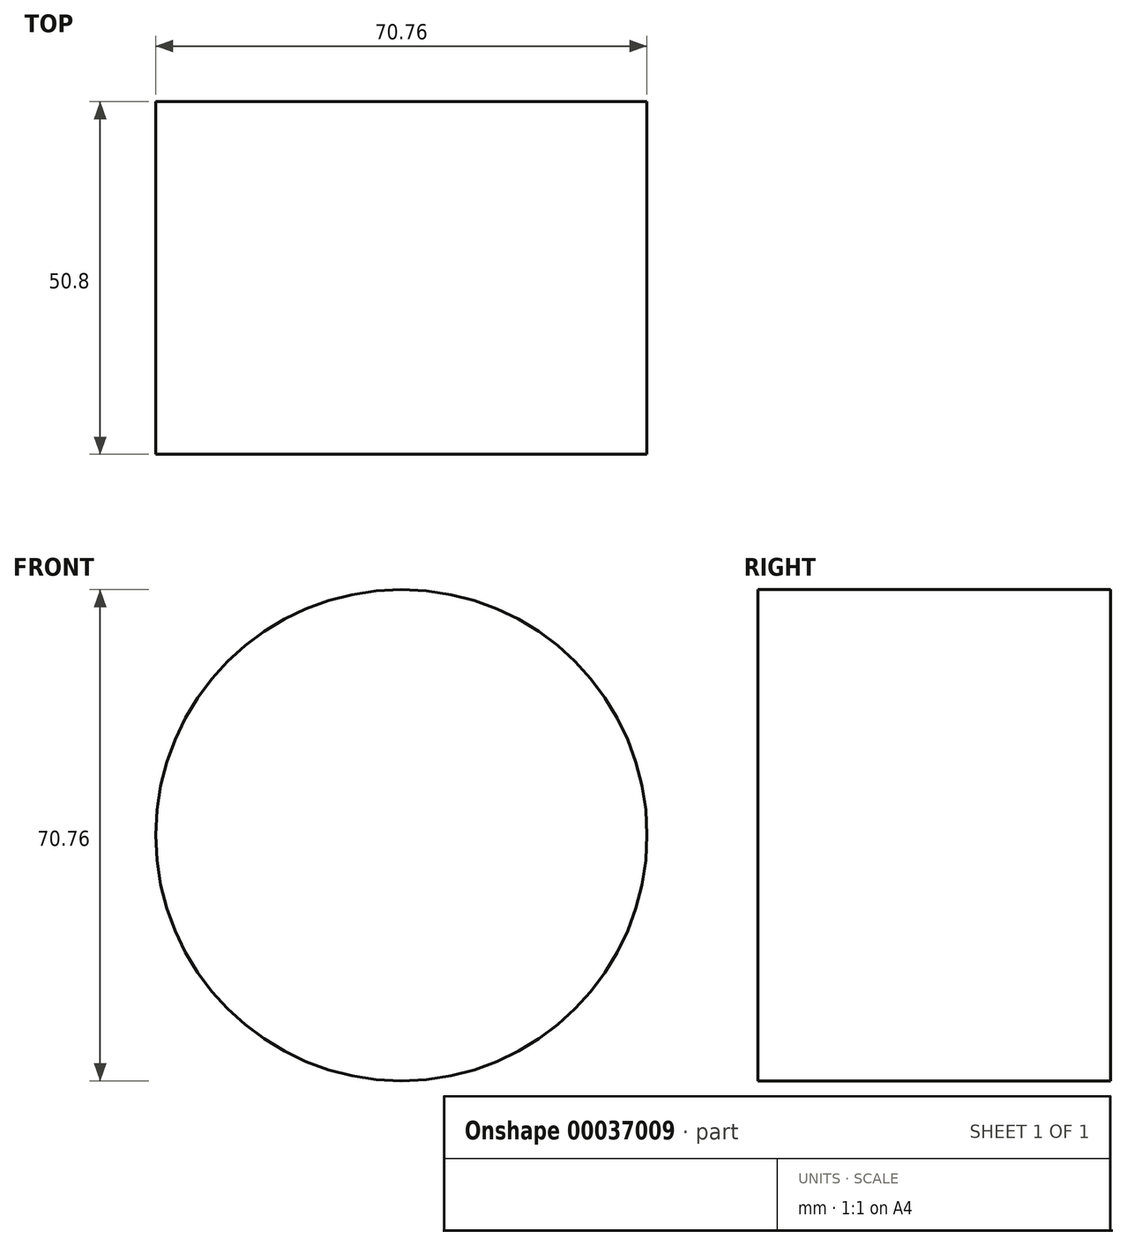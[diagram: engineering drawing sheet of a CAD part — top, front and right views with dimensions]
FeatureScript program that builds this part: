
annotation { "Feature Type Name" : "Feature", "Feature Type Description" : "" }
export const myFeature = defineFeature(function(context is Context, id is Id, definition is map)
    precondition{}
    {
        {
            var Q0;
            Q0=qCreatedBy(makeId("Front.planeOp"),FACE);
            var sketch = newSketch(context, id + "F0", { "sketchPlane" : qUnion([Q0])});
            skCircle(sketch, "E0", {"center": v(0, 0) * mm, "radius": 35.38 * mm});
            skCircle(sketch, "E1.cCircle", {"center": v(0, 0) * mm, "radius": 29.9 * mm, "construction": true});
            skLineSegment(sketch, "E1.0", {"start": v(17.26, -29.9) * mm, "end": v(-17.26, -29.9) * mm});
            skLineSegment(sketch, "E1.1", {"start": v(-17.26, -29.9) * mm, "end": v(-34.53, 0) * mm});
            skLineSegment(sketch, "E1.2", {"start": v(-34.53, 0) * mm, "end": v(-17.26, 29.9) * mm});
            skLineSegment(sketch, "E1.3", {"start": v(-17.26, 29.9) * mm, "end": v(17.26, 29.9) * mm});
            skLineSegment(sketch, "E1.4", {"start": v(17.26, 29.9) * mm, "end": v(34.53, 0) * mm});
            skLineSegment(sketch, "E1.5", {"start": v(34.53, 0) * mm, "end": v(17.26, -29.9) * mm});
            skPoint(sketch, "E1.0.midPoint", {"position": v(0, -29.9) * mm});
            skSolve(sketch);
        }
        {
            var Q0;
            Q0=makeQuery(id+"F0.imprint","IMPRINT",FACE,{"disambiguationData":[TD([[makeQuery(id+"F0.imprint","IMPRINT",EDGE,{"derivedFrom":sQuery(id+"F0.wireOp",EDGE,"E0")}),1.0]])]});
            var Q1;
            Q1=makeQuery(id+"F0.imprint","IMPRINT",FACE,{"disambiguationData":[TD([[makeQuery(id+"F0.imprint","IMPRINT",EDGE,{"derivedFrom":sQuery(id+"F0.wireOp",EDGE,"E1.0")}),-1.0]])]});
            extrude(context, id + "F1", {"entities" : qUnion([Q0, Q1]), "depth" : 50.8 * mm});
        }
    });
